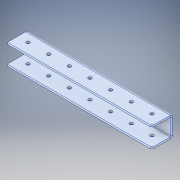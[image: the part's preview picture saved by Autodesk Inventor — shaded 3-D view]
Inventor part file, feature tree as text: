
AUTODESK INVENTOR PART (.ipt)
format: ipt  version: 2017 (Build 210142000, 142)  size: 244,736 bytes
history: native  units: in
note: dims shown in document units (in); Inventor stores cm internally (conversion verified against a paired STEP export)
features: split x1, sketch x1, other x1
ambient origin geometry x8: Origin, YZ Plane, XZ Plane, XY Plane, X Axis, Y Axis, Z Axis, Center Point
bodies: Solid1 (feature_tree)
feature tree (3):
  split  "Split1"
  sketch  "Sketch1"
  other  "Break-Corner1"
